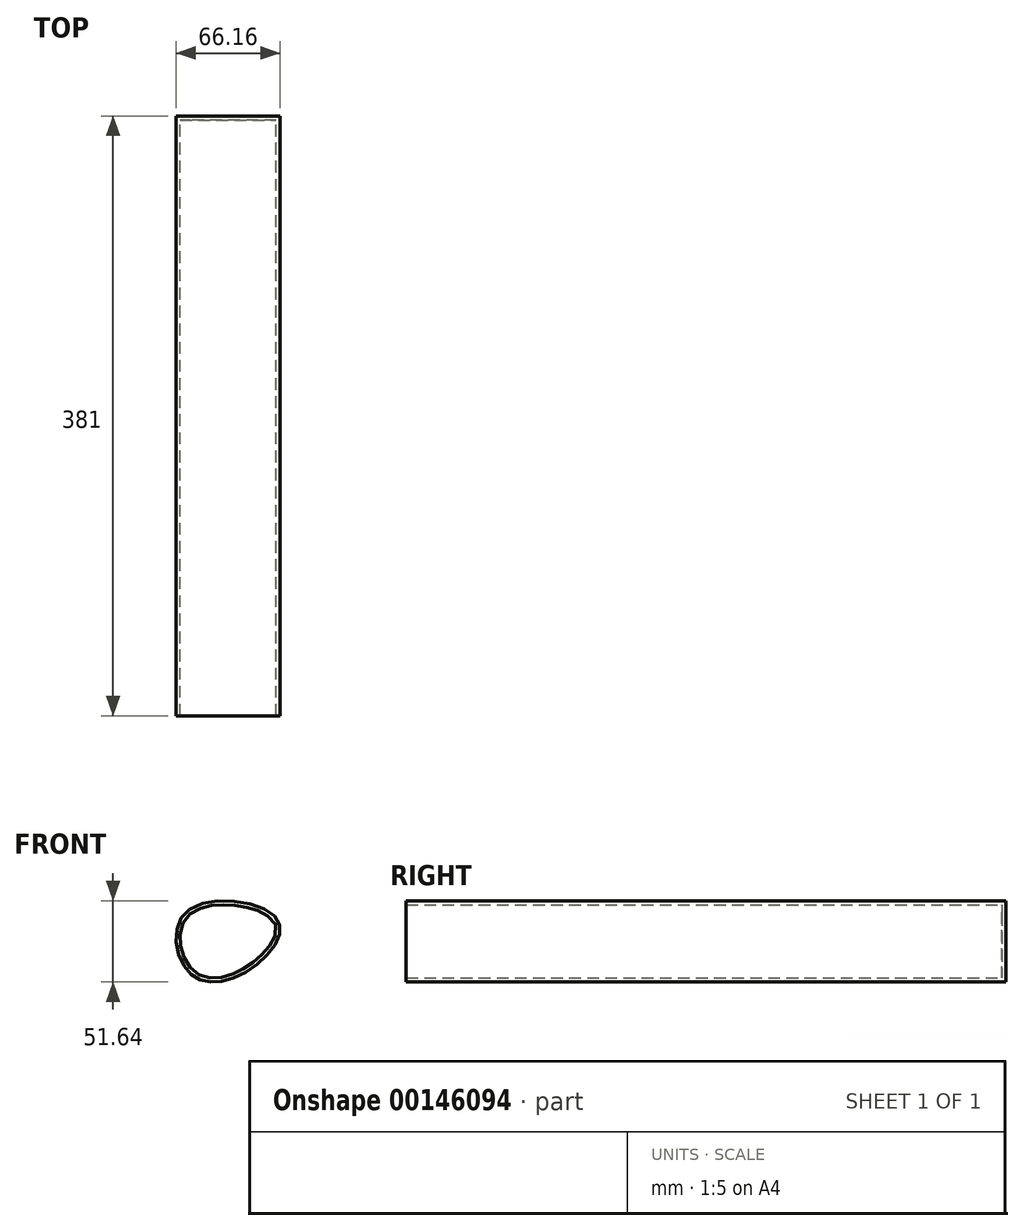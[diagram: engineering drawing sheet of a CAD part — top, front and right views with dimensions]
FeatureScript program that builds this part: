
annotation { "Feature Type Name" : "Feature", "Feature Type Description" : "" }
export const myFeature = defineFeature(function(context is Context, id is Id, definition is map)
    precondition{}
    {
        {
            var Q0;
            Q0=qCreatedBy(makeId("Front.planeOp"),FACE);
            var sketch = newSketch(context, id + "F0", { "sketchPlane" : qUnion([Q0])});
            skFitSpline(sketch, "E0", {"points": [v(0, 0) * mm, v(20.58, 33.13) * mm, v(-36.65, 39.07) * mm, v(-35.77, 0) * mm, v(0, 0) * mm]});
            skSolve(sketch);
        }
        {
            var Q0;
            Q0=makeQuery(id+"F0.imprint","IMPRINT",FACE,{"disambiguationData":[TD([[makeQuery(id+"F0.imprint","IMPRINT",EDGE,{"derivedFrom":sQuery(id+"F0.wireOp",EDGE,"E0")}),1.0]])]});
            extrude(context, id + "F1", {"entities" : qUnion([Q0]), "depth" : 381 * mm});
        }
        {
            var Q0;
            Q0=makeQuery(id+"F1.opExtrude","CAP_FACE",FACE,{"disambiguationData":[OSD([sQuery(id+"F0.wireOp",EDGE,"E0")])],"isStart":false});
            shell(context, id + "F2", {"entities" : qUnion([Q0]), "thickness" : 2.54 * mm});
        }
    });
